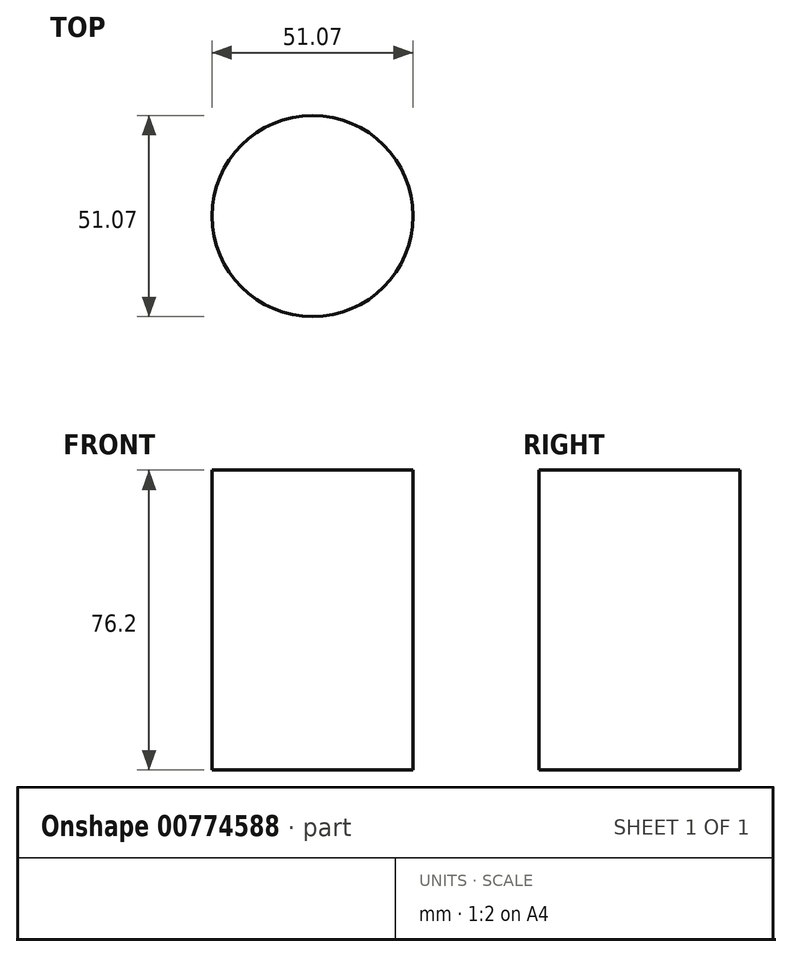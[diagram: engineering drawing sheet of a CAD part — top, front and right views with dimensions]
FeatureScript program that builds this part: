
annotation { "Feature Type Name" : "Feature", "Feature Type Description" : "" }
export const myFeature = defineFeature(function(context is Context, id is Id, definition is map)
    precondition{}
    {
        {
            var Q0;
            Q0=qCreatedBy(makeId("Top.planeOp"),FACE);
            var sketch = newSketch(context, id + "F0", { "sketchPlane" : qUnion([Q0])});
            skCircle(sketch, "E0", {"center": v(-29.08, 16.93) * mm, "radius": 25.53 * mm});
            skSolve(sketch);
        }
        {
            var Q0;
            Q0=makeQuery(id+"F0.imprint","IMPRINT",FACE,{"disambiguationData":[TD([[makeQuery(id+"F0.imprint","IMPRINT",EDGE,{"derivedFrom":sQuery(id+"F0.wireOp",EDGE,"E0")}),1.0]])]});
            extrude(context, id + "F1", {"entities" : qUnion([Q0]), "depth" : 76.2 * mm, "offsetDistance" : 25.4 * mm});
        }
    });
